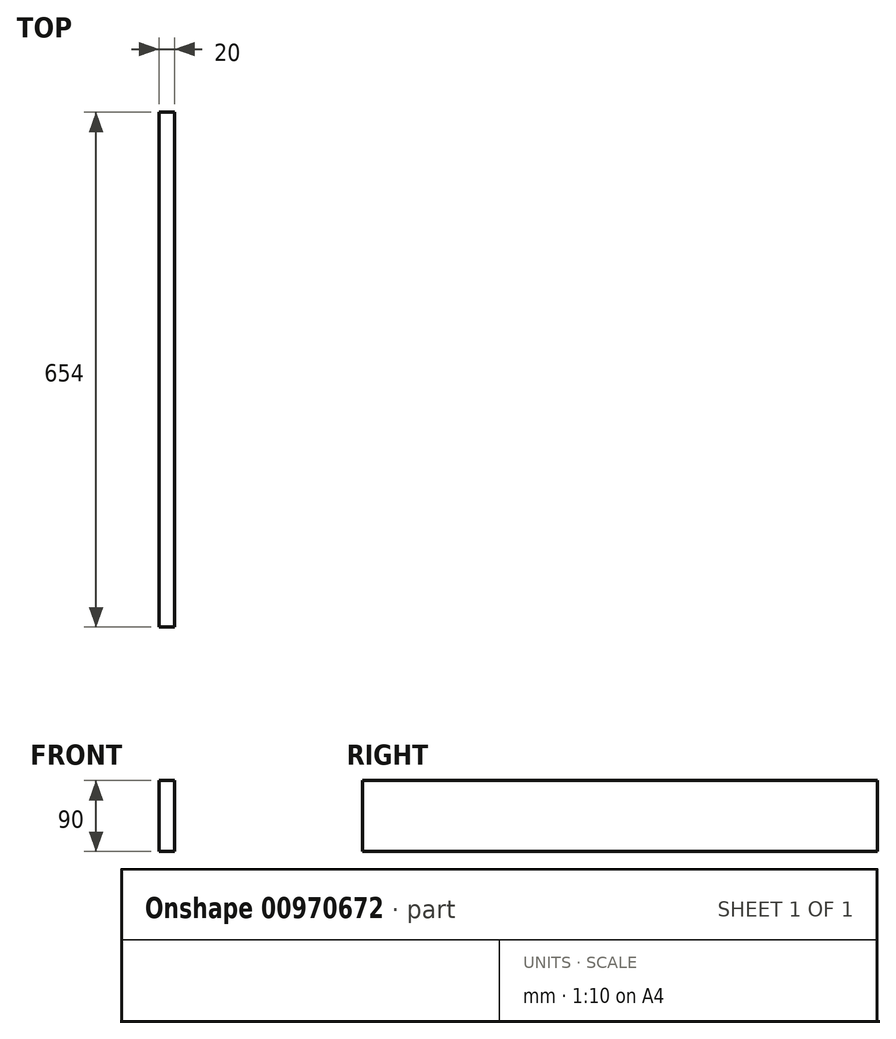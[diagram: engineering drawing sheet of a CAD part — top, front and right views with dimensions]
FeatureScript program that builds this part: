
annotation { "Feature Type Name" : "Feature", "Feature Type Description" : "" }
export const myFeature = defineFeature(function(context is Context, id is Id, definition is map)
    precondition{}
    {
        {
            var Q0;
            Q0=qCreatedBy(makeId("Front.planeOp"),FACE);
            var sketch = newSketch(context, id + "F0", { "sketchPlane" : qUnion([Q0])});
            skLineSegment(sketch, "E0.bottom", {"start": v(-6.84, 83.55) * mm, "end": v(13.16, 83.55) * mm});
            skLineSegment(sketch, "E0.top", {"start": v(-6.84, -6.45) * mm, "end": v(13.16, -6.45) * mm});
            skLineSegment(sketch, "E0.left", {"start": v(-6.84, 83.55) * mm, "end": v(-6.84, -6.45) * mm});
            skLineSegment(sketch, "E0.right", {"start": v(13.16, 83.55) * mm, "end": v(13.16, -6.45) * mm});
            skSolve(sketch);
        }
        {
            var Q0;
            Q0 = qSketchRegion(id + "F0", true);
            extrude(context, id + "F1", {"entities" : qUnion([Q0]), "depth" : 654 * mm, "offsetDistance" : 25 * mm});
        }
    });
